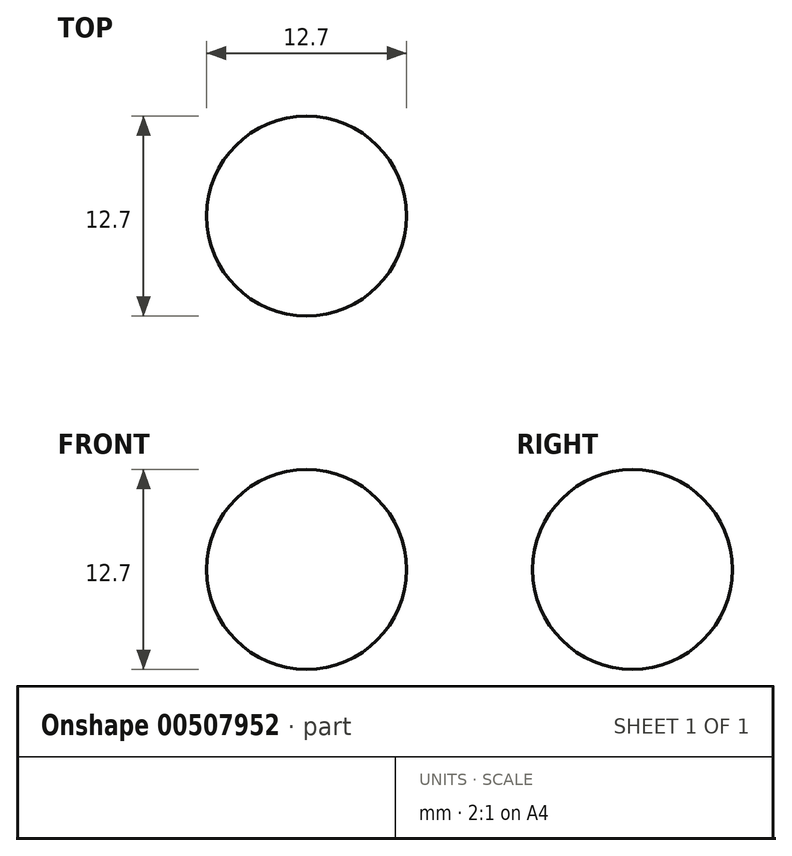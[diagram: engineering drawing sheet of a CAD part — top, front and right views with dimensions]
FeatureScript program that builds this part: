
annotation { "Feature Type Name" : "Feature", "Feature Type Description" : "" }
export const myFeature = defineFeature(function(context is Context, id is Id, definition is map)
    precondition{}
    {
        {
            var Q0;
            Q0=qCreatedBy(makeId("Front.planeOp"),FACE);
            var sketch = newSketch(context, id + "F0", { "sketchPlane" : qUnion([Q0])});
            skArc(sketch, "E0", {"start": v(0, 6.35) * mm, "mid": v(-6.35, 0) * mm, "end": v(0, -6.35) * mm});
            skLineSegment(sketch, "E1", {"start": v(0, -6.35) * mm, "end": v(0, 6.35) * mm});
            skSolve(sketch);
        }
        {
            var Q0;
            Q0=makeQuery(id+"F0.imprint","IMPRINT",FACE,{"disambiguationData":[TD([[makeQuery(id+"F0.imprint","IMPRINT",EDGE,{"derivedFrom":sQuery(id+"F0.wireOp",EDGE,"E0")}),1.0]])]});
            var Q1;
            Q1=sQuery(id+"F0.wireOp",EDGE,"E1");
            revolve(context, id + "F1", {"entities" : qUnion([Q0]), "axis" : qUnion([Q1]), "revolveType" : RevolveType.FULL});
        }
    });
